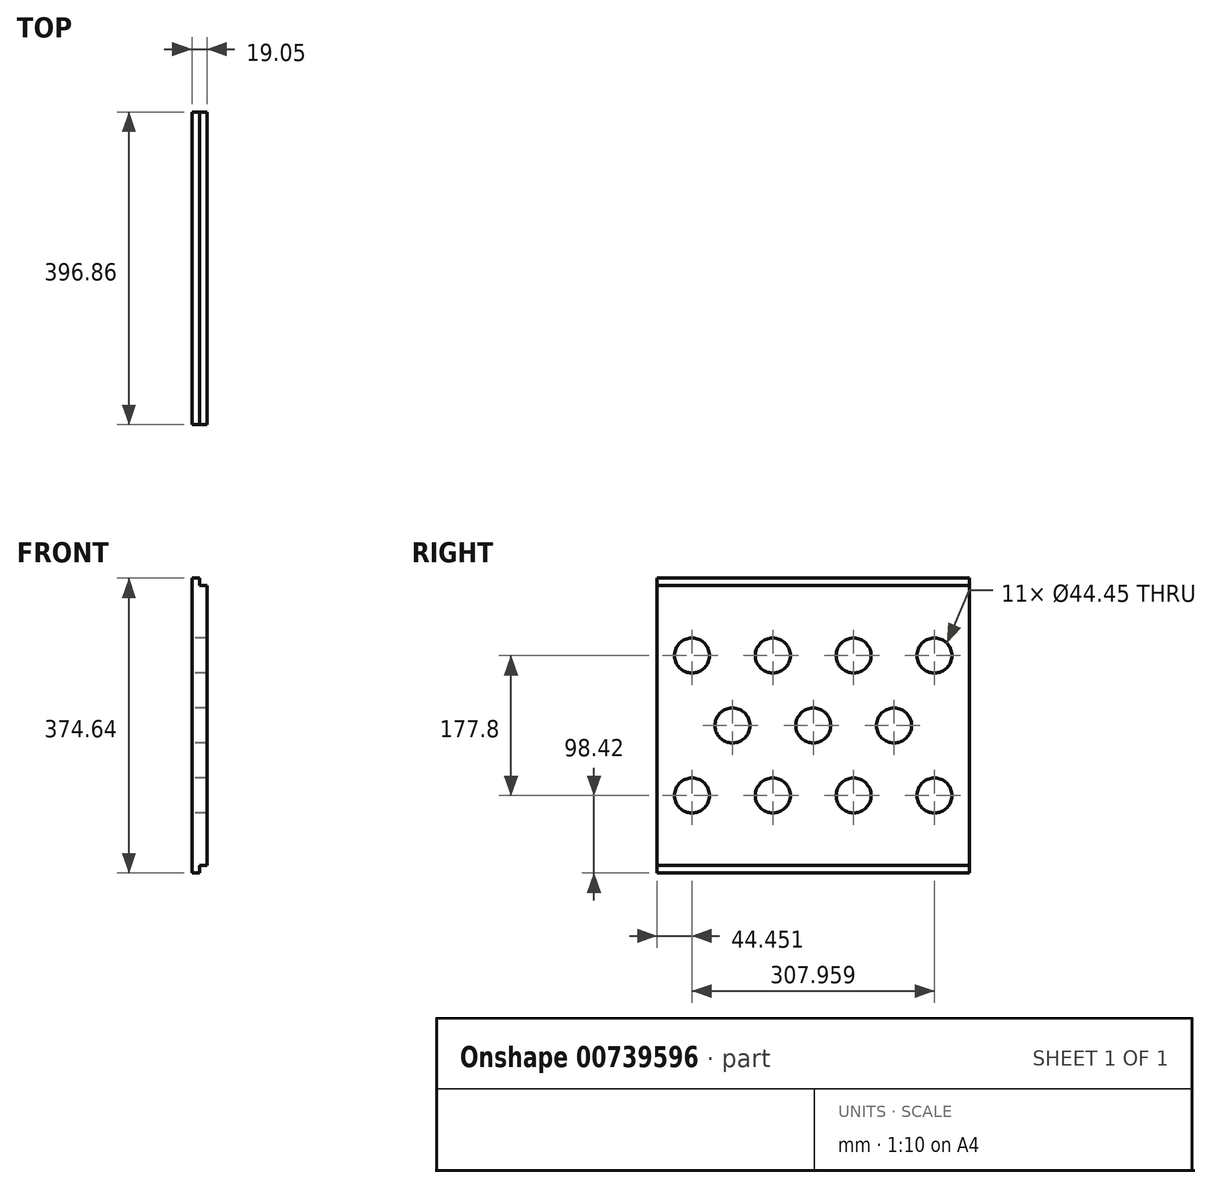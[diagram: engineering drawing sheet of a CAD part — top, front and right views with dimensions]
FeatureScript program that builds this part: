
annotation { "Feature Type Name" : "Feature", "Feature Type Description" : "" }
export const myFeature = defineFeature(function(context is Context, id is Id, definition is map)
    precondition{}
    {
        {
            var Q0;
            Q0=qCreatedBy(makeId("Right.planeOp"),FACE);
            var sketch = newSketch(context, id + "F0", { "sketchPlane" : qUnion([Q0])});
            skLineSegment(sketch, "E0", {"start": v(0, 1143) * mm, "end": v(0, -1143) * mm, "construction": true});
            skLineSegment(sketch, "E1.0", {"start": v(198.43, 1143) * mm, "end": v(198.43, -390.52) * mm, "construction": true});
            skLineSegment(sketch, "E2.bottom", {"start": v(198.43, -22.23) * mm, "end": v(-198.43, -22.23) * mm, "construction": true});
            skLineSegment(sketch, "E2.top", {"start": v(198.43, 22.23) * mm, "end": v(-198.43, 22.23) * mm, "construction": true});
            skLineSegment(sketch, "E2.left", {"start": v(198.43, -22.23) * mm, "end": v(198.43, 22.23) * mm, "construction": true});
            skLineSegment(sketch, "E2.right", {"start": v(-198.43, -22.23) * mm, "end": v(-198.43, 22.23) * mm, "construction": true});
            skPoint(sketch, "E2.middle", {"position": v(0, 0) * mm});
            skLineSegment(sketch, "E3.0", {"start": v(127, -66.68) * mm, "end": v(-127, -66.68) * mm, "construction": true});
            skLineSegment(sketch, "E4.0", {"start": v(127, 66.68) * mm, "end": v(-127, 66.68) * mm, "construction": true});
            skCircle(sketch, "E5", {"center": v(0, 0) * mm, "radius": 22.23 * mm});
            skLineSegment(sketch, "E6", {"start": v(0, 0) * mm, "end": v(51.33, 88.9) * mm, "construction": true});
            skLineSegment(sketch, "E7.0", {"start": v(127, 88.9) * mm, "end": v(-127, 88.9) * mm, "construction": true});
            skCircle(sketch, "E8", {"center": v(51.33, 88.9) * mm, "radius": 22.22 * mm});
            skLineSegment(sketch, "E9", {"start": v(51.33, 88.9) * mm, "end": v(51.33, -22.23) * mm, "construction": true});
            skCircle(sketch, "E10.MirrorC", {"center": v(102.65, 0) * mm, "radius": 22.23 * mm});
            skLineSegment(sketch, "E11", {"start": v(102.65, 0) * mm, "end": v(102.65, 88.9) * mm, "construction": true});
            skCircle(sketch, "E12.MirrorC", {"center": v(153.98, 88.9) * mm, "radius": 22.22 * mm});
            skCircle(sketch, "E13.MirrorC", {"center": v(-51.33, 88.9) * mm, "radius": 22.22 * mm});
            skCircle(sketch, "E14.MirrorC", {"center": v(-153.98, 88.9) * mm, "radius": 22.22 * mm});
            skCircle(sketch, "E15.MirrorC", {"center": v(-102.65, 0) * mm, "radius": 22.23 * mm});
            skLineSegment(sketch, "E16.MirrorCS", {"start": v(-198.43, 1143) * mm, "end": v(-198.43, -390.52) * mm, "construction": true});
            skCircle(sketch, "E17.MirrorC", {"center": v(-153.98, -88.9) * mm, "radius": 22.22 * mm});
            skCircle(sketch, "E18.MirrorC", {"center": v(-51.33, -88.9) * mm, "radius": 22.22 * mm});
            skCircle(sketch, "E19.MirrorC", {"center": v(51.33, -88.9) * mm, "radius": 22.22 * mm});
            skCircle(sketch, "E20.MirrorC", {"center": v(153.98, -88.9) * mm, "radius": 22.22 * mm});
            skCircle(sketch, "E21.MirrorC", {"center": v(0, 177.8) * mm, "radius": 22.23 * mm, "construction": true});
            skLineSegment(sketch, "E22.bottom", {"start": v(198.43, 187.32) * mm, "end": v(-198.43, 187.32) * mm, "construction": true});
            skLineSegment(sketch, "E22.top", {"start": v(198.43, 168.28) * mm, "end": v(-198.43, 168.28) * mm, "construction": true});
            skLineSegment(sketch, "E22.left", {"start": v(198.43, 187.32) * mm, "end": v(198.43, 168.28) * mm, "construction": true});
            skLineSegment(sketch, "E22.right", {"start": v(-198.43, 187.32) * mm, "end": v(-198.43, 168.28) * mm, "construction": true});
            skCircle(sketch, "E23.MirrorC", {"center": v(0, -177.8) * mm, "radius": 22.23 * mm, "construction": true});
            skLineSegment(sketch, "E24.bottom", {"start": v(198.43, -187.32) * mm, "end": v(-198.43, -187.32) * mm, "construction": true});
            skLineSegment(sketch, "E24.top", {"start": v(198.43, -168.27) * mm, "end": v(-198.43, -168.27) * mm, "construction": true});
            skLineSegment(sketch, "E24.left", {"start": v(198.43, -187.32) * mm, "end": v(198.43, -168.27) * mm, "construction": true});
            skLineSegment(sketch, "E24.right", {"start": v(-198.43, -187.32) * mm, "end": v(-198.43, -168.27) * mm, "construction": true});
            skLineSegment(sketch, "E25.bottom", {"start": v(198.43, 177.8) * mm, "end": v(-198.43, 177.8) * mm});
            skLineSegment(sketch, "E25.top", {"start": v(198.43, -177.8) * mm, "end": v(-198.43, -177.8) * mm});
            skLineSegment(sketch, "E25.left", {"start": v(198.43, 177.8) * mm, "end": v(198.43, -177.8) * mm});
            skLineSegment(sketch, "E25.right", {"start": v(-198.43, 177.8) * mm, "end": v(-198.43, -177.8) * mm});
            skSolve(sketch);
        }
        {
            var Q0;
            Q0=qSketchRegion(id+"F0",true);
            extrude(context, id + "F1", {"entities" : qUnion([Q0]), "depth" : 19.05 * mm, "offsetDistance" : 25.4 * mm});
        }
        {
            var Q0;
            Q0=makeQuery(id+"F1.opExtrude","SWEPT_FACE",FACE,{"disambiguationData":[OSD([sQuery(id+"F0.wireOp",EDGE,"E25.bottom")])]});
            var sketch = newSketch(context, id + "F2", { "sketchPlane" : qUnion([Q0])});
            skLineSegment(sketch, "E26.bottom", {"start": v(0, -198.43) * mm, "end": v(9.53, -198.43) * mm});
            skLineSegment(sketch, "E26.top", {"start": v(0, 198.43) * mm, "end": v(9.53, 198.43) * mm});
            skLineSegment(sketch, "E26.left", {"start": v(0, -198.43) * mm, "end": v(0, 198.43) * mm});
            skLineSegment(sketch, "E26.right", {"start": v(9.53, -198.43) * mm, "end": v(9.53, 198.43) * mm});
            skSolve(sketch);
        }
        {
            var Q0;
            Q0 = qSketchRegion(id + "F2", true);
            extrude(context, id + "F3", {"entities" : qUnion([Q0]), "operationType" : NewBodyOperationType.ADD, "depth" : 9.52 * mm, "offsetDistance" : 25.4 * mm});
        }
        {
            var Q0;
            Q0=makeQuery(id+"F1.opExtrude","SWEPT_FACE",FACE,{"disambiguationData":[OSD([sQuery(id+"F0.wireOp",EDGE,"E25.top")])]});
            var sketch = newSketch(context, id + "F4", { "sketchPlane" : qUnion([Q0])});
            skLineSegment(sketch, "E27.bottom", {"start": v(9.52, 198.43) * mm, "end": v(0, 198.43) * mm});
            skLineSegment(sketch, "E27.top", {"start": v(9.53, -198.43) * mm, "end": v(0, -198.43) * mm});
            skLineSegment(sketch, "E27.left", {"start": v(9.53, 198.43) * mm, "end": v(9.53, -198.43) * mm});
            skLineSegment(sketch, "E27.right", {"start": v(0, 198.43) * mm, "end": v(0, -198.43) * mm});
            skSolve(sketch);
        }
        {
            var Q0;
            Q0 = qSketchRegion(id + "F4", true);
            extrude(context, id + "F5", {"entities" : qUnion([Q0]), "operationType" : NewBodyOperationType.ADD, "depth" : 9.52 * mm, "offsetDistance" : 25.4 * mm});
        }
    });
